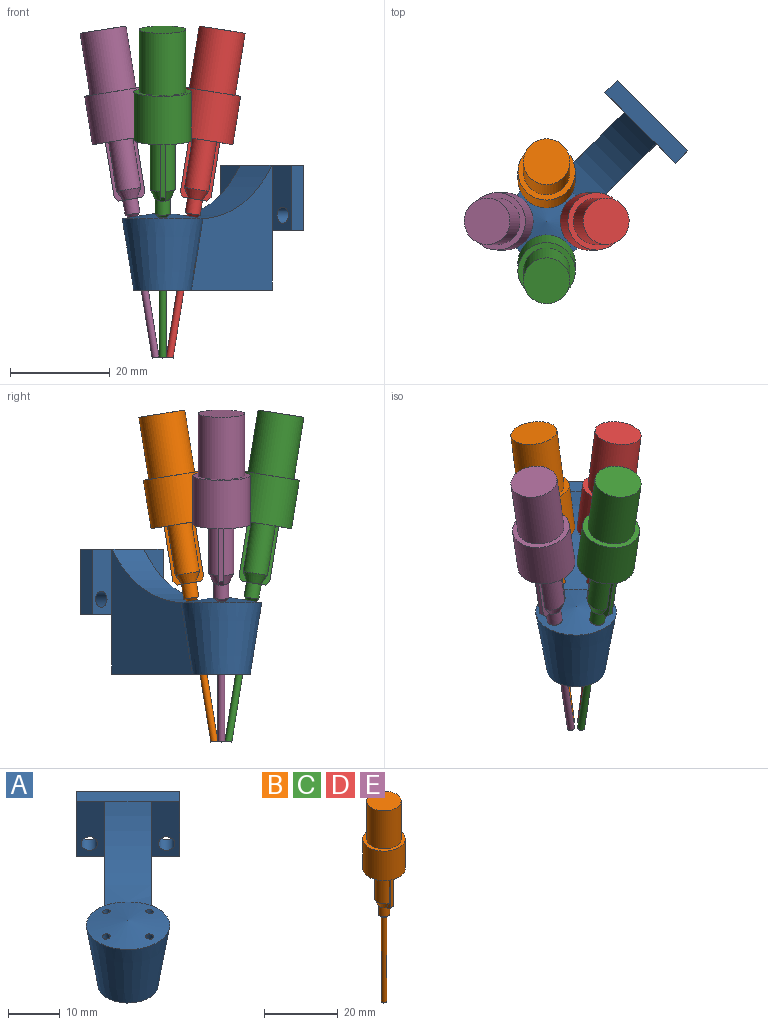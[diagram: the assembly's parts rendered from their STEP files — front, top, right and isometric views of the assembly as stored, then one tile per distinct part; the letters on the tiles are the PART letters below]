
ASSEMBLY  parts=5 mates=1
PART A: 20 faces, bbox 36.9x36.9x25.7 mm
  f0: plane 11.95x6.36mm, normal (0.71,0.71,0), area 107.5mm2, adj f6,f7,f10,f19
  f1: cone r=8.09mm half-angle=9.1deg, axis (0,0,1), area 485mm2, adj f6,f7,f8,f19
  f2: cylinder r=0.75mm len=15mm, axis (-0.16,0,-0.99), area 69.9mm2, adj f8,f19
  f3: cylinder r=0.75mm len=15mm, axis (0,0.16,-0.99), area 70.5mm2, adj f8,f19
  f4: cylinder r=0.75mm len=15mm, axis (0,-0.16,-0.99), area 69.9mm2, adj f8,f19
  f5: cylinder r=0.75mm len=15mm, axis (0.16,0,-0.99), area 70.5mm2, adj f8,f19
  f6: plane 25.47x16.62mm, normal (0.71,-0.71,0), area 368.2mm2, adj f0,f1,f8,f9,f18,f19
  f7: plane 25.47x16.62mm, normal (-0.71,0.71,0), area 368.2mm2, adj f0,f1,f8,f9,f11,f19
  f8: cone r=0mm half-angle=80.9deg, axis (0,0,-1), area 199.2mm2, adj f1,f2,f3,f4,f5,f6,f7,f9
  f9: cylinder r=24.49mm len=20.37mm, axis (-0.71,0.71,0), area 203.7mm2, adj f6,f7,f8,f14
  f10: plane 16.62x16.62mm, normal (0,0,-1), area 70mm2, adj f0,f11,f12,f13,f15,f18
  f11: plane 13.05x3.89mm, normal (-0.71,-0.71,0), area 63.7mm2, adj f7,f10,f13,f14,f17
  f12: plane 14.14x14.14mm, normal (0.71,0.71,0), area 244.9mm2, adj f10,f13,f14,f15,f16,f17
  f13: plane 13.05x2.48mm, normal (-0.71,0.71,0), area 45.7mm2, adj f10,f11,f12,f14
  f14: plane 16.62x16.62mm, normal (0,0,1), area 70mm2, adj f9,f11,f12,f13,f15,f18
  f15: plane 13.05x2.48mm, normal (0.71,-0.71,0), area 45.7mm2, adj f10,f12,f14,f18
  f16: cylinder r=1.6mm len=4.74mm, axis (-0.71,-0.71,0), area 35.2mm2, adj f12,f18
  f17: cylinder r=1.6mm len=4.74mm, axis (-0.71,-0.71,0), area 35.2mm2, adj f11,f12
  f18: plane 13.05x3.89mm, normal (-0.71,-0.71,0), area 63.7mm2, adj f6,f10,f14,f15,f16
  f19: plane 28.2x28.2mm, normal (0,0,-1), area 290.7mm2, adj f0,f1,f2,f3,f4,f5,f6,f7
PART B: 27 faces, bbox 11.6x11.6x66.6 mm
  f0: plane 1x0.91mm, normal (0,0,-1), area 0.9mm2, adj f3,f5,f11,f21
  f1: plane 12.07x1.78mm, normal (-1,0,0), area 8.8mm2, adj f2,f8,f9,f12,f18,f20
  f2: cylinder r=2.5mm len=10mm, axis (0,0,-1), area 68.5mm2, adj f1,f3,f12,f18
  f3: plane 12.07x1.78mm, normal (-1,0,0), area 8.8mm2, adj f0,f2,f4,f12,f18,f21
  f4: plane 11.2x1mm, normal (0,-1,0), area 11.2mm2, adj f3,f5,f12,f21
  f5: plane 12.07x1.78mm, normal (1,0,0), area 8.8mm2, adj f0,f4,f6,f12,f19,f21
  f6: cylinder r=2.5mm len=10mm, axis (0,0,-1), area 68.5mm2, adj f5,f7,f12,f19
  f7: plane 12.07x1.78mm, normal (1,0,0), area 8.8mm2, adj f6,f8,f9,f12,f19,f20
  f8: plane 11.2x1mm, normal (0,1,0), area 11.2mm2, adj f1,f7,f12,f20
  f9: plane 1x0.91mm, normal (0,0,-1), area 0.9mm2, adj f1,f7,f11,f20
  f10: plane 1.8x1.8mm, normal (0,0,-1), area 1mm2, adj f15,f16
  f11: cylinder r=1.5mm len=3mm, axis (0,0,1), area 28.3mm2, adj f0,f9,f15,f18,f19
  f12: plane 11.5x11.5mm, normal (0,0,-1), area 83mm2, adj f1,f2,f3,f4,f5,f6,f7,f8
  f13: cylinder r=5.75mm len=11.5mm, axis (0,0,-1), area 354.1mm2, adj f12,f14
  f14: plane 11.5x11.5mm, normal (0,0,1), area 35.9mm2, adj f13,f22
  f15: cone r=0.9mm half-angle=45deg, axis (0,0,1), area 6.4mm2, adj f10,f11
  f16: cylinder r=0.7mm len=28.5mm, axis (0,0,1), area 125.3mm2, adj f10,f17
  f17: plane 1.4x1.4mm, normal (0,0,-1), area 1.5mm2, adj f16
  f18: cone r=2.5mm half-angle=26.6deg, axis (0,0,1), area 11.7mm2, adj f1,f2,f3,f11
  f19: cone r=2.5mm half-angle=26.6deg, axis (0,0,1), area 11.7mm2, adj f5,f6,f7,f11
  f20: plane 1x0.8mm, normal (0,0.71,-0.71), area 1.1mm2, adj f1,f7,f8,f9
  f21: plane 1x0.8mm, normal (0,-0.71,-0.71), area 1.1mm2, adj f0,f3,f4,f5
  f22: cylinder r=4.65mm len=12.6mm, axis (0,0,-1), area 368.1mm2, adj f14,f23
  f23: plane 9.3x9.3mm, normal (0,0,1), area 67.9mm2, adj f22
  f24: plane 0.12x0.12mm, normal (0,0,1), area 0mm2, adj f25
  f25: cylinder r=0.06mm len=12mm, axis (0,0,-1), area 4.5mm2, adj f24,f26
  f26: plane 0.12x0.12mm, normal (0,0,-1), area 0mm2, adj f25
PART C: same geometry as B
PART D: same geometry as B
PART E: same geometry as B
PLACE A t=(-13.67,2.38,-13.07)mm
PLACE B rot(axis=(0,-0.08,-1),180deg) t=(-13.67,8.87,27.5)mm
PLACE C rot(axis=(1,0,0),9.1deg) t=(-13.67,-4.12,27.5)mm
PLACE D rot(axis=(0.08,0.08,0.99),90.4deg) t=(-7.17,2.38,27.5)mm
PLACE E rot(axis=(0.08,-0.08,-0.99),90.4deg) t=(-20.16,2.38,27.5)mm
MATE fastened C.f16 <-> A.f3  axis (0,0.16,-0.99) through (-13.67,-3.55,23.95)mm
